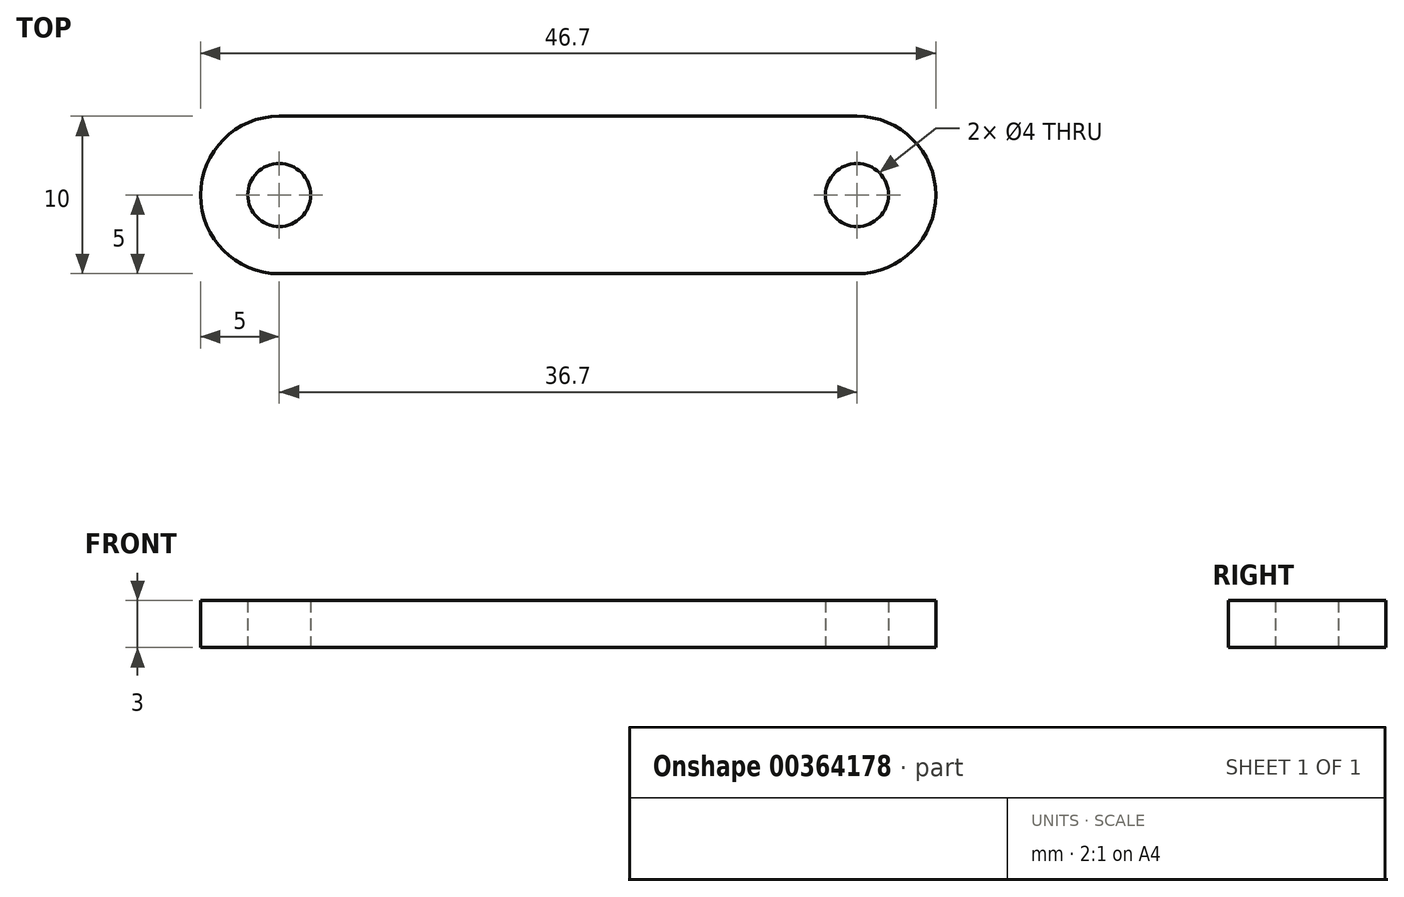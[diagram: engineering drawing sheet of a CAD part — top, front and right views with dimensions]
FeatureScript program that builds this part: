
annotation { "Feature Type Name" : "Feature", "Feature Type Description" : "" }
export const myFeature = defineFeature(function(context is Context, id is Id, definition is map)
    precondition{}
    {
        {
            var Q0;
            Q0=qCreatedBy(makeId("Top.planeOp"),FACE);
            var sketch = newSketch(context, id + "F0", { "sketchPlane" : qUnion([Q0])});
            skLineSegment(sketch, "E0.bottom", {"start": v(18.35, 5) * mm, "end": v(-18.35, 5) * mm});
            skLineSegment(sketch, "E0.top", {"start": v(18.35, -5) * mm, "end": v(-18.35, -5) * mm});
            skPoint(sketch, "E0.middle", {"position": v(0, 0) * mm});
            skCircle(sketch, "E1", {"center": v(-18.35, 0) * mm, "radius": 2 * mm});
            skCircle(sketch, "E2", {"center": v(18.35, 0) * mm, "radius": 2 * mm});
            skArc(sketch, "E3", {"start": v(-18.35, 5) * mm, "mid": v(-23.35, 0) * mm, "end": v(-18.35, -5) * mm});
            skArc(sketch, "E4", {"start": v(18.35, -5) * mm, "mid": v(23.35, 0) * mm, "end": v(18.35, 5) * mm});
            skSolve(sketch);
        }
        {
            var Q0;
            Q0=qSketchRegion(id+"F0",true);
            extrude(context, id + "F1", {"entities" : qUnion([Q0]), "depth" : 3 * mm});
        }
    });
